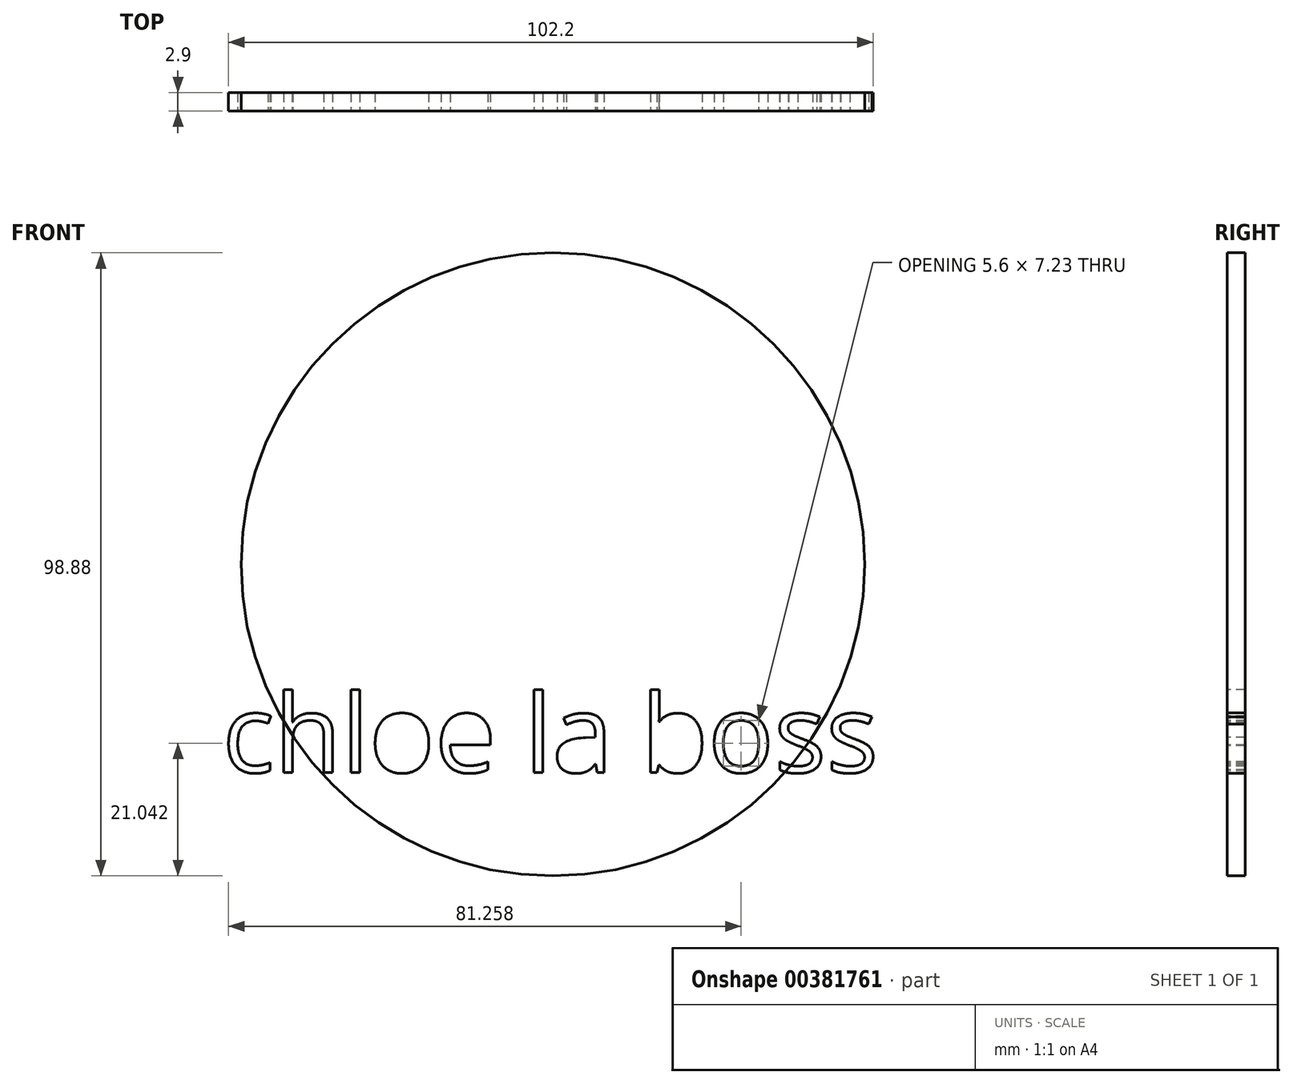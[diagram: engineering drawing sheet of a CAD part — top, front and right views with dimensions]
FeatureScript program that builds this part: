
annotation { "Feature Type Name" : "Feature", "Feature Type Description" : "" }
export const myFeature = defineFeature(function(context is Context, id is Id, definition is map)
    precondition{}
    {
        {
            var Q0;
            Q0=qCreatedBy(makeId("Front.planeOp"),FACE);
            var sketch = newSketch(context, id + "F0", { "sketchPlane" : qUnion([Q0])});
            skCircle(sketch, "E0", {"center": v(0, 0) * mm, "radius": 49.44 * mm});
            skSolve(sketch);
        }
        {
            var Q0;
            Q0=qCreatedBy(makeId("Front.planeOp"),FACE);
            var sketch = newSketch(context, id + "F1", { "sketchPlane" : qUnion([Q0])});
            skText(sketch, "E1", { "text": "chloe la boss", "fontName": "OpenSans-Regular.ttf"});
            const initialGuessF1  = {"E1": [-0.0524, -0.03302, 1, 0, 0.01246]};
            skSetInitialGuess(sketch, initialGuessF1);
            skSolve(sketch);
        }
        {
            var Q0;
            Q0=makeQuery(id+"F1.imprint","IMPRINT",FACE,{"disambiguationData":[TD([[makeQuery(id+"F1.imprint","IMPRINT",EDGE,{"derivedFrom":sQuery(id+"F1.wireOp",EDGE,"E1.sketch_text.stroke-0")}),-1.0]])]});
            var Q1;
            Q1=makeQuery(id+"F1.imprint","IMPRINT",FACE,{"disambiguationData":[TD([[makeQuery(id+"F1.imprint","IMPRINT",EDGE,{"derivedFrom":sQuery(id+"F1.wireOp",EDGE,"E1.sketch_text.stroke-15")}),-1.0]])]});
            var Q2;
            Q2=makeQuery(id+"F1.imprint","IMPRINT",FACE,{"disambiguationData":[TD([[makeQuery(id+"F1.imprint","IMPRINT",EDGE,{"derivedFrom":sQuery(id+"F1.wireOp",EDGE,"E1.sketch_text.stroke-33")}),-1.0]])]});
            var Q3;
            Q3=makeQuery(id+"F1.imprint","IMPRINT",FACE,{"disambiguationData":[TD([[makeQuery(id+"F1.imprint","IMPRINT",EDGE,{"derivedFrom":sQuery(id+"F1.wireOp",EDGE,"E1.sketch_text.stroke-73")}),-1.0]])]});
            var Q4;
            Q4=makeQuery(id+"F1.imprint","IMPRINT",FACE,{"disambiguationData":[TD([[makeQuery(id+"F1.imprint","IMPRINT",EDGE,{"derivedFrom":sQuery(id+"F1.wireOp",EDGE,"E1.sketch_text.stroke-144")}),-1.0]])]});
            var Q5;
            Q5=makeQuery(id+"F1.imprint","IMPRINT",FACE,{"disambiguationData":[TD([[makeQuery(id+"F1.imprint","IMPRINT",EDGE,{"derivedFrom":sQuery(id+"F1.wireOp",EDGE,"E1.sketch_text.stroke-169")}),-1.0]])]});
            var Q6;
            Q6=makeQuery(id+"F1.imprint","IMPRINT",FACE,{"disambiguationData":[TD([[makeQuery(id+"F1.imprint","IMPRINT",EDGE,{"derivedFrom":sQuery(id+"F1.wireOp",EDGE,"E1.sketch_text.stroke-37")}),-1.0]])]});
            var Q7;
            Q7=makeQuery(id+"F1.imprint","IMPRINT",FACE,{"disambiguationData":[TD([[makeQuery(id+"F1.imprint","IMPRINT",EDGE,{"derivedFrom":sQuery(id+"F1.wireOp",EDGE,"E1.sketch_text.stroke-54")}),-1.0]])]});
            var Q8;
            Q8=makeQuery(id+"F1.imprint","IMPRINT",FACE,{"disambiguationData":[TD([[makeQuery(id+"F1.imprint","IMPRINT",EDGE,{"derivedFrom":sQuery(id+"F1.wireOp",EDGE,"E1.sketch_text.stroke-77")}),-1.0]])]});
            var Q9;
            Q9=makeQuery(id+"F1.imprint","IMPRINT",FACE,{"disambiguationData":[TD([[makeQuery(id+"F1.imprint","IMPRINT",EDGE,{"derivedFrom":sQuery(id+"F1.wireOp",EDGE,"E1.sketch_text.stroke-104")}),-1.0]])]});
            var Q10;
            Q10=makeQuery(id+"F1.imprint","IMPRINT",FACE,{"disambiguationData":[TD([[makeQuery(id+"F1.imprint","IMPRINT",EDGE,{"derivedFrom":sQuery(id+"F1.wireOp",EDGE,"E1.sketch_text.stroke-127")}),-1.0]])]});
            var Q11;
            Q11=makeQuery(id+"F0.imprint","IMPRINT",FACE,{"disambiguationData":[TD([[makeQuery(id+"F0.imprint","IMPRINT",EDGE,{"derivedFrom":sQuery(id+"F0.wireOp",EDGE,"E0")}),1.0]])]});
            var Q12;
            Q12=makeQuery(id+"F1.imprint","IMPRINT",FACE,{"disambiguationData":[TD([[makeQuery(id+"F1.imprint","IMPRINT",EDGE,{"derivedFrom":sQuery(id+"F1.wireOp",EDGE,"E1.sketch_text.stroke-46")}),1.0]])]});
            var Q13;
            Q13=makeQuery(id+"F1.imprint","IMPRINT",FACE,{"disambiguationData":[TD([[makeQuery(id+"F1.imprint","IMPRINT",EDGE,{"derivedFrom":sQuery(id+"F1.wireOp",EDGE,"E1.sketch_text.stroke-68")}),1.0]])]});
            var Q14;
            Q14=makeQuery(id+"F1.imprint","IMPRINT",FACE,{"disambiguationData":[TD([[makeQuery(id+"F1.imprint","IMPRINT",EDGE,{"derivedFrom":sQuery(id+"F1.wireOp",EDGE,"E1.sketch_text.stroke-96")}),1.0]])]});
            var Q15;
            Q15 = qSketchRegion(id + "F1", true);
            var Q16;
            Q16=makeQuery(id+"F1.imprint","IMPRINT",FACE,{"disambiguationData":[TD([[makeQuery(id+"F1.imprint","IMPRINT",EDGE,{"derivedFrom":sQuery(id+"F1.wireOp",EDGE,"E1.sketch_text.stroke-119")}),1.0]])]});
            extrude(context, id + "F2", {"entities" : qUnion([Q0, Q1, Q2, Q3, Q4, Q5, Q6, Q7, Q8, Q9, Q10, Q11, Q12, Q13, Q14, Q15, Q16]), "oppositeDirection" : true, "depth" : 2.9 * mm});
        }
    });
